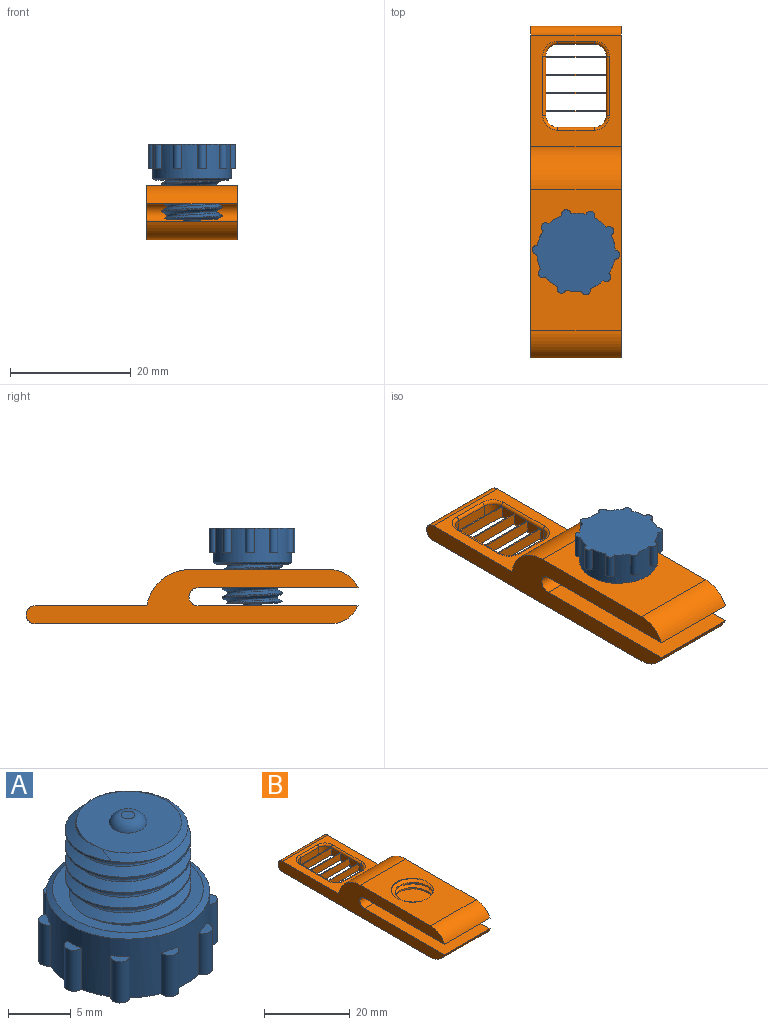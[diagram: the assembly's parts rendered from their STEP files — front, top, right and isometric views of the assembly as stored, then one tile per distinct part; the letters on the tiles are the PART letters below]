
ASSEMBLY  parts=2 mates=1
PART A: 32 faces, bbox 14.9x14.5x13.6 mm
  f0: cylinder r=6.5mm len=13mm, axis (0,0,-1), area 173.2mm2, adj f3,f9,f10,f11,f12,f13,f14,f15
  f1: cylinder r=5mm len=10mm, axis (0,0,-1), area 22.5mm2, adj f2,f6,f7,f8
  f2: plane 12.42x12.42mm, normal (0,0,1), area 48.3mm2, adj f1,f5,f6,f7,f31
  f3: plane 14.48x14.09mm, normal (0,0,-1), area 141.8mm2, adj f0,f9,f11,f13,f15,f17,f19,f21
  f4: plane 8.56x8.47mm, normal (0,0,1), area 48.9mm2, adj f5,f6,f7,f8,f30
  f5: bspline ~9.67x8.38mm, area 47.3mm2, adj f2,f4,f6,f7
  f6: bspline ~11.55x10mm, area 114mm2, adj f1,f2,f4,f5,f8
  f7: bspline ~11.55x10mm, area 114.3mm2, adj f1,f2,f4,f5,f8
  f8: cone r=5mm half-angle=63.4deg, axis (0,0,-1), area 9.9mm2, adj f1,f4,f6,f7
  f9: cylinder r=0.75mm len=4mm, axis (0,0,-1), area 9.8mm2, adj f0,f3,f10
  f10: plane 1.36x1.26mm, normal (0,0,1), area 0.9mm2, adj f0,f9
  f11: cylinder r=0.75mm len=4mm, axis (0,0,-1), area 9.8mm2, adj f0,f3,f12
  f12: plane 1.46x1.06mm, normal (0,0,1), area 0.9mm2, adj f0,f11
  f13: cylinder r=0.75mm len=4mm, axis (0,0,-1), area 9.8mm2, adj f0,f3,f14
  f14: plane 1.5x0.84mm, normal (0,0,1), area 0.9mm2, adj f0,f13
  f15: cylinder r=0.75mm len=4mm, axis (0,0,-1), area 9.8mm2, adj f0,f3,f16
  f16: plane 1.49x0.98mm, normal (0,0,1), area 0.9mm2, adj f0,f15
  f17: cylinder r=0.75mm len=4mm, axis (0,0,-1), area 9.8mm2, adj f0,f3,f18
  f18: plane 1.46x1.06mm, normal (0,0,1), area 0.9mm2, adj f0,f17
  f19: cylinder r=0.75mm len=4mm, axis (0,0,-1), area 9.8mm2, adj f0,f3,f20
  f20: plane 1.5x0.84mm, normal (0,0,1), area 0.9mm2, adj f0,f19
  f21: cylinder r=0.75mm len=4mm, axis (0,0,-1), area 9.8mm2, adj f0,f3,f22
  f22: plane 1.4x1.19mm, normal (0,0,1), area 0.9mm2, adj f0,f21
  f23: cylinder r=0.75mm len=4mm, axis (0,0,-1), area 9.8mm2, adj f0,f3,f24
  f24: plane 1.49x0.98mm, normal (0,0,1), area 0.9mm2, adj f0,f23
  f25: cylinder r=0.75mm len=4mm, axis (0,0,-1), area 9.8mm2, adj f0,f3,f26
  f26: plane 1.36x1.26mm, normal (0,0,1), area 0.9mm2, adj f0,f25
  f27: cylinder r=0.75mm len=4mm, axis (0,0,-1), area 9.8mm2, adj f0,f3,f28
  f28: plane 1.4x1.19mm, normal (0,0,1), area 0.9mm2, adj f0,f27
  f29: plane 1.09x1.09mm, normal (0,0,1), area 0.9mm2, adj f30
  f30: torus R=0.55mm, axis (0,0,-1), area 8.7mm2, adj f4,f29
  f31: cone r=6mm half-angle=60deg, axis (0,0,-1), area 22.7mm2, adj f0,f2
PART B: 64 faces, bbox 15.4x55.4x10 mm
  f0: plane 2x0.59mm, normal (1,0,0), area 1.2mm2, adj f18,f35,f43,f61
  f1: plane 2.8x2mm, normal (-1,0,0), area 5.6mm2, adj f36,f44,f57,f63
  f2: plane 2.8x2mm, normal (1,0,0), area 5.6mm2, adj f35,f43,f57,f63
  f3: plane 2.8x2mm, normal (-1,0,0), area 5.6mm2, adj f36,f44,f53,f59
  f4: plane 2.8x2mm, normal (1,0,0), area 5.6mm2, adj f35,f43,f53,f59
  f5: plane 2.8x2mm, normal (-1,0,0), area 5.6mm2, adj f36,f44,f49,f55
  f6: plane 26.94x15.44mm, normal (0,0,-1), area 323mm2, adj f10,f11,f21,f22,f23,f24,f28,f30
  f7: plane 23.73x15.44mm, normal (0,0,1), area 274.7mm2, adj f10,f11,f21,f22,f23,f24,f27,f28
  f8: plane 48.92x15mm, normal (0,0,-1), area 576.4mm2, adj f10,f11,f29,f31,f40,f41,f42,f43
  f9: plane 18.5x15mm, normal (0,0,1), area 120.2mm2, adj f10,f11,f27,f31,f32,f33,f34,f35
  f10: plane 55x9mm, normal (1,0,0), area 272.8mm2, adj f6,f7,f8,f9,f12,f27,f28,f29
  f11: plane 55x9mm, normal (-1,0,0), area 272.8mm2, adj f6,f7,f8,f9,f12,f27,f28,f29
  f12: plane 26.5x15mm, normal (0,0,1), area 390.4mm2, adj f10,f11,f26,f29,f30
  f13: plane 6x2mm, normal (0,-1,0), area 12mm2, adj f17,f20,f32,f40
  f14: plane 2.8x2mm, normal (1,0,0), area 5.6mm2, adj f35,f43,f49,f55
  f15: plane 6x2mm, normal (0,1,0), area 12mm2, adj f18,f19,f39,f47
  f16: plane 2x0.59mm, normal (-1,0,0), area 1.2mm2, adj f19,f36,f44,f61
  f17: cylinder r=2mm len=2mm, axis (0,0,1), area 6.3mm2, adj f13,f33,f41,f51
  f18: cylinder r=2mm len=2mm, axis (0,0,-1), area 6.3mm2, adj f0,f15,f37,f45
  f19: cylinder r=2mm len=2mm, axis (0,0,1), area 6.3mm2, adj f15,f16,f38,f46
  f20: cylinder r=2mm len=2mm, axis (0,0,-1), area 6.3mm2, adj f13,f34,f42,f51
  f21: bspline ~12.27x10.62mm, area 57.9mm2, adj f6,f7,f23,f24
  f22: bspline ~12.27x10.62mm, area 57.8mm2, adj f6,f7,f23,f24
  f23: bspline ~12.42x10.76mm, area 14.6mm2, adj f6,f7,f21,f22
  f24: cylinder r=4.5mm len=9mm, axis (0,0,-1), area 21.2mm2, adj f6,f7,f21,f22
  f25: plane 1.09x1.09mm, normal (0,0,1), area 0.9mm2, adj f26
  f26: torus R=0.55mm, axis (0,0,-1), area 8.7mm2, adj f12,f25
  f27: cylinder r=7.24mm len=15mm, axis (1,0,0), area 151.9mm2, adj f7,f9,f10,f11
  f28: cylinder r=5mm len=15mm, axis (1,0,0), area 86.9mm2, adj f6,f7,f10,f11
  f29: cylinder r=5mm len=15mm, axis (-1,0,0), area 86.9mm2, adj f8,f10,f11,f12
  f30: cylinder r=1.5mm len=15mm, axis (-1,0,0), area 70.7mm2, adj f6,f10,f11,f12
  f31: cylinder r=1.5mm len=15mm, axis (1,0,0), area 70.7mm2, adj f8,f9,f10,f11
  f32: cylinder r=0.5mm len=6mm, axis (-1,0,0), area 4.7mm2, adj f9,f13,f33,f34
  f33: torus R=2.5mm, axis (0,0,-1), area 2.7mm2, adj f9,f17,f32,f35
  f34: torus R=2.5mm, axis (0,0,-1), area 2.7mm2, adj f9,f20,f32,f36
  f35: cylinder r=0.5mm len=9.79mm, axis (0,-1,0), area 7.7mm2, adj f0,f2,f4,f9,f14,f33,f37,f50
  f36: cylinder r=0.5mm len=9.79mm, axis (0,1,0), area 7.7mm2, adj f1,f3,f5,f9,f16,f34,f38,f50
  f37: torus R=2.5mm, axis (0,0,-1), area 2.7mm2, adj f9,f18,f35,f39
  f38: torus R=2.5mm, axis (0,0,-1), area 2.7mm2, adj f9,f19,f36,f39
  f39: cylinder r=0.5mm len=6mm, axis (1,0,0), area 4.7mm2, adj f9,f15,f37,f38
  f40: cylinder r=0.5mm len=6mm, axis (-1,0,0), area 4.7mm2, adj f8,f13,f41,f42
  f41: torus R=2.5mm, axis (0,0,1), area 2.7mm2, adj f8,f17,f40,f43
  f42: torus R=2.5mm, axis (0,0,1), area 2.7mm2, adj f8,f20,f40,f44
  f43: cylinder r=0.5mm len=9.79mm, axis (0,-1,0), area 7.7mm2, adj f0,f2,f4,f8,f14,f41,f45,f48
  f44: cylinder r=0.5mm len=9.79mm, axis (0,1,0), area 7.7mm2, adj f1,f3,f5,f8,f16,f42,f46,f48
  f45: torus R=2.5mm, axis (0,0,1), area 2.7mm2, adj f8,f18,f43,f47
  f46: torus R=2.5mm, axis (0,0,1), area 2.7mm2, adj f8,f19,f44,f47
  f47: cylinder r=0.5mm len=6mm, axis (1,0,0), area 4.7mm2, adj f8,f15,f45,f46
  f48: plane 10x0.2mm, normal (0,0,-1), area 2mm2, adj f43,f44,f49,f51
  f49: plane 10x2mm, normal (0,-1,0), area 20mm2, adj f5,f14,f48,f50
  f50: plane 10x0.2mm, normal (0,0,1), area 2mm2, adj f35,f36,f49,f51
  f51: plane 10x2mm, normal (0,1,0), area 20mm2, adj f17,f20,f48,f50
  f52: plane 10x0.2mm, normal (0,0,-1), area 2mm2, adj f43,f44,f53,f55
  f53: plane 10x2mm, normal (0,-1,0), area 20mm2, adj f3,f4,f52,f54
  f54: plane 10x0.2mm, normal (0,0,1), area 2mm2, adj f35,f36,f53,f55
  f55: plane 10x2mm, normal (0,1,0), area 20mm2, adj f5,f14,f52,f54
  f56: plane 10x0.2mm, normal (0,0,-1), area 2mm2, adj f43,f44,f57,f59
  f57: plane 10x2mm, normal (0,-1,0), area 20mm2, adj f1,f2,f56,f58
  f58: plane 10x0.2mm, normal (0,0,1), area 2mm2, adj f35,f36,f57,f59
  f59: plane 10x2mm, normal (0,1,0), area 20mm2, adj f3,f4,f56,f58
  f60: plane 10x0.2mm, normal (0,0,-1), area 2mm2, adj f43,f44,f61,f63
  f61: plane 10x2mm, normal (0,-1,0), area 20mm2, adj f0,f16,f60,f62
  f62: plane 10x0.2mm, normal (0,0,1), area 2mm2, adj f35,f36,f61,f63
  f63: plane 10x2mm, normal (0,1,0), area 20mm2, adj f1,f2,f60,f62
PLACE A rot(axis=(0,1,0),180deg) t=(-40.74,-5.04,3)mm
PLACE B t=(0,0,-12.9)mm
MATE slider A.f0 <-> B.f26  axis (0,0,1) through (0,0,3)mm
